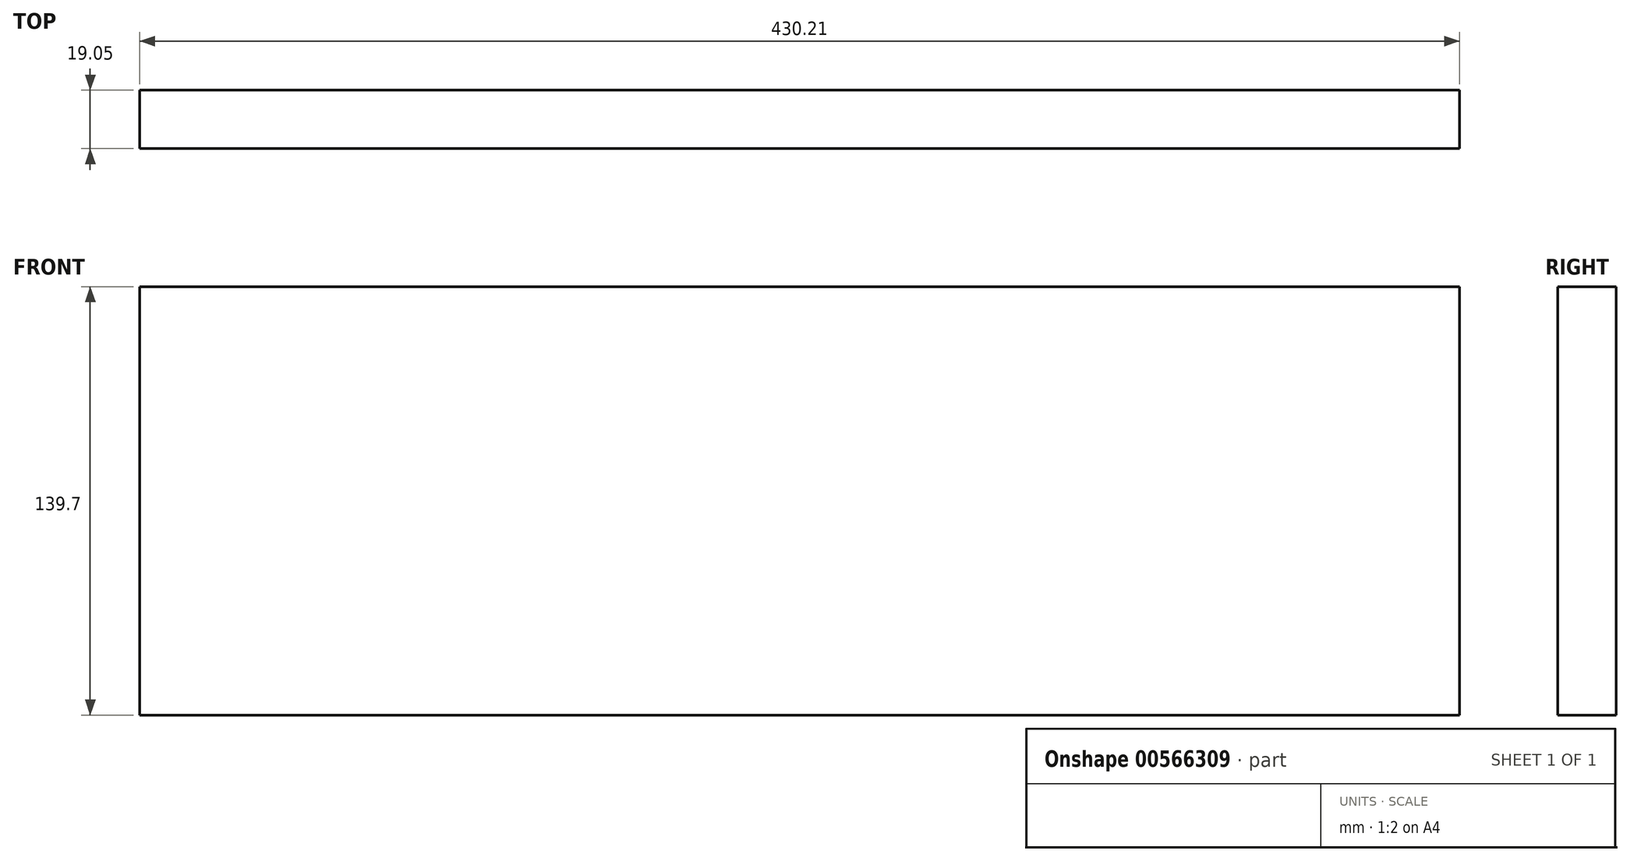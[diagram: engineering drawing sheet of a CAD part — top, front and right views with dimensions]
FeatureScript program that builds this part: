
annotation { "Feature Type Name" : "Feature", "Feature Type Description" : "" }
export const myFeature = defineFeature(function(context is Context, id is Id, definition is map)
    precondition{}
    {
        {
            var Q0;
            Q0=qCreatedBy(makeId("Front.planeOp"),FACE);
            var sketch = newSketch(context, id + "F0", { "sketchPlane" : qUnion([Q0])});
            skLineSegment(sketch, "E0.bottom", {"start": v(0, 0) * mm, "end": v(430.21, 0) * mm});
            skLineSegment(sketch, "E0.top", {"start": v(0, 139.7) * mm, "end": v(430.21, 139.7) * mm});
            skLineSegment(sketch, "E0.left", {"start": v(0, 0) * mm, "end": v(0, 139.7) * mm});
            skLineSegment(sketch, "E0.right", {"start": v(430.21, 0) * mm, "end": v(430.21, 139.7) * mm});
            skSolve(sketch);
        }
        {
            var Q0;
            Q0=makeQuery(id+"F0.imprint","IMPRINT",FACE,{"disambiguationData":[TD([[makeQuery(id+"F0.imprint","IMPRINT",EDGE,{"derivedFrom":sQuery(id+"F0.wireOp",EDGE,"E0.bottom")}),1.0]])]});
            extrude(context, id + "F1", {"entities" : qUnion([Q0]), "depth" : 19.05 * mm, "offsetDistance" : 25.4 * mm});
        }
    });
